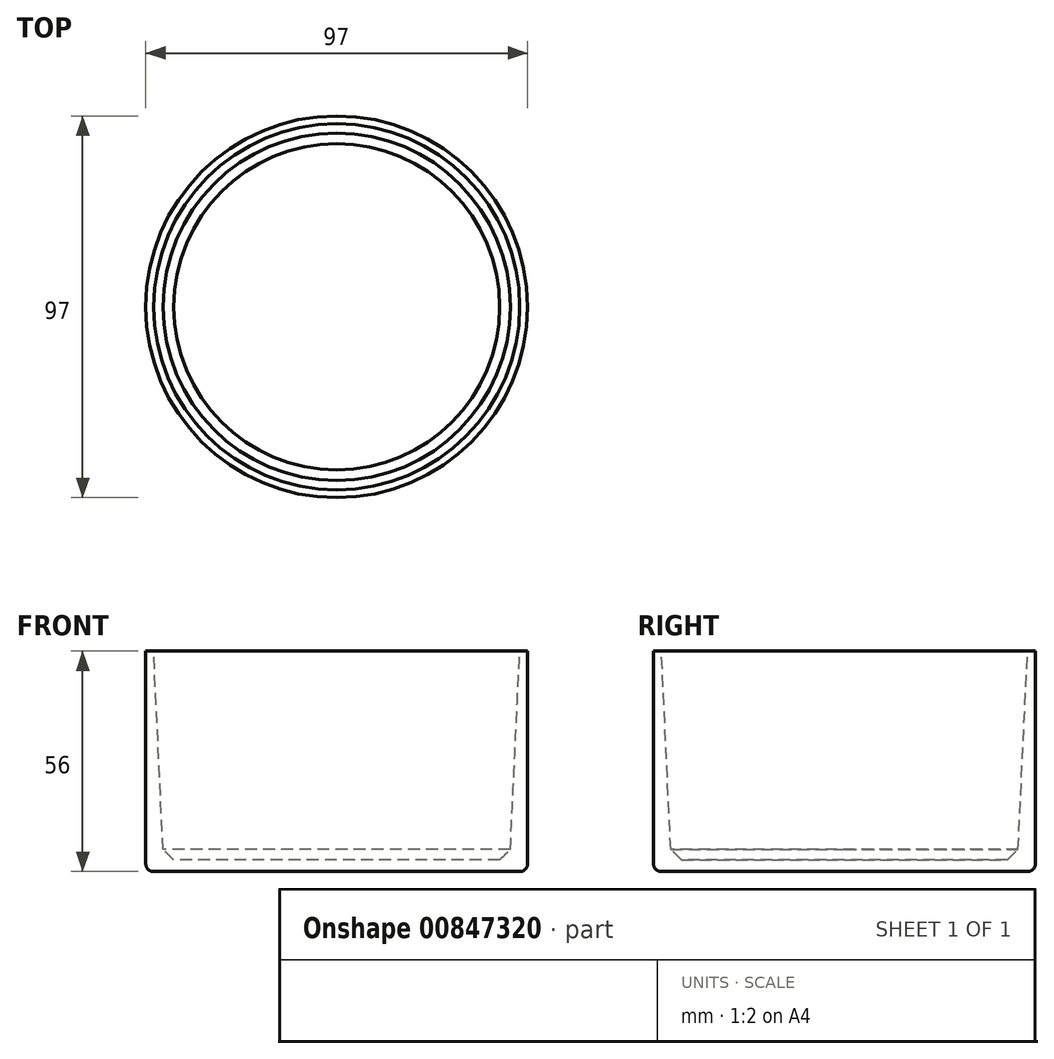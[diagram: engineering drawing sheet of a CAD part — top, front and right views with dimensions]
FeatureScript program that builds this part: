
annotation { "Feature Type Name" : "Feature", "Feature Type Description" : "" }
export const myFeature = defineFeature(function(context is Context, id is Id, definition is map)
    precondition{}
    {
        {
            var Q0;
            Q0=qCreatedBy(makeId("Front.planeOp"),FACE);
            var sketch = newSketch(context, id + "F0", { "sketchPlane" : qUnion([Q0])});
            skLineSegment(sketch, "E0", {"start": v(0, 0) * mm, "end": v(-46.5, 0) * mm});
            skLineSegment(sketch, "E1", {"start": v(-48.5, 2) * mm, "end": v(-48.5, 56) * mm});
            skLineSegment(sketch, "E2", {"start": v(-48.5, 56) * mm, "end": v(-46.5, 56) * mm});
            skLineSegment(sketch, "E3", {"start": v(-46.5, 56) * mm, "end": v(-44, 3.06) * mm});
            skLineSegment(sketch, "E4", {"start": v(-44, 3) * mm, "end": v(0, 3) * mm});
            skLineSegment(sketch, "E5", {"start": v(0, 3) * mm, "end": v(0, 0) * mm});
            skLineSegment(sketch, "E6", {"start": v(-44, 3.06) * mm, "end": v(-44, 3) * mm});
            skPoint(sketch, "E7.visualSharp", {"position": v(-48.5, 0) * mm});
            skArc(sketch, "E7.filletArc", {"start": v(-48.5, 2) * mm, "mid": v(-47.91, 0.59) * mm, "end": v(-46.5, 0) * mm});
            skLineSegment(sketch, "E8", {"start": v(-44.12, 5.59) * mm, "end": v(-41.4, 3) * mm});
            skSolve(sketch);
        }
        {
            var Q0;
            {var subQ0=sQuery(id+"F0.wireOp",EDGE,"E6");Q0=makeQuery(id+"F0.imprint","IMPRINT",FACE,{"disambiguationData":[TD([[makeQuery(id+"F0.imprint","IMPRINT",EDGE,{"derivedFrom":subQ0}),1.0]])]});}
            var Q1;
            Q1=makeQuery(id+"F0.imprint","IMPRINT",FACE,{"disambiguationData":[TD([[makeQuery(id+"F0.imprint","IMPRINT",EDGE,{"derivedFrom":sQuery(id+"F0.wireOp",EDGE,"E0")}),-1.0]])]});
            var Q2;
            Q2=sQuery(id+"F0.wireOp",EDGE,"E5");
            revolve(context, id + "F1", {"surfaceOperationType" : NewSurfaceOperationType.NEW, "entities" : qUnion([Q0, Q1]), "axis" : qUnion([Q2]), "revolveType" : RevolveType.FULL});
        }
    });
